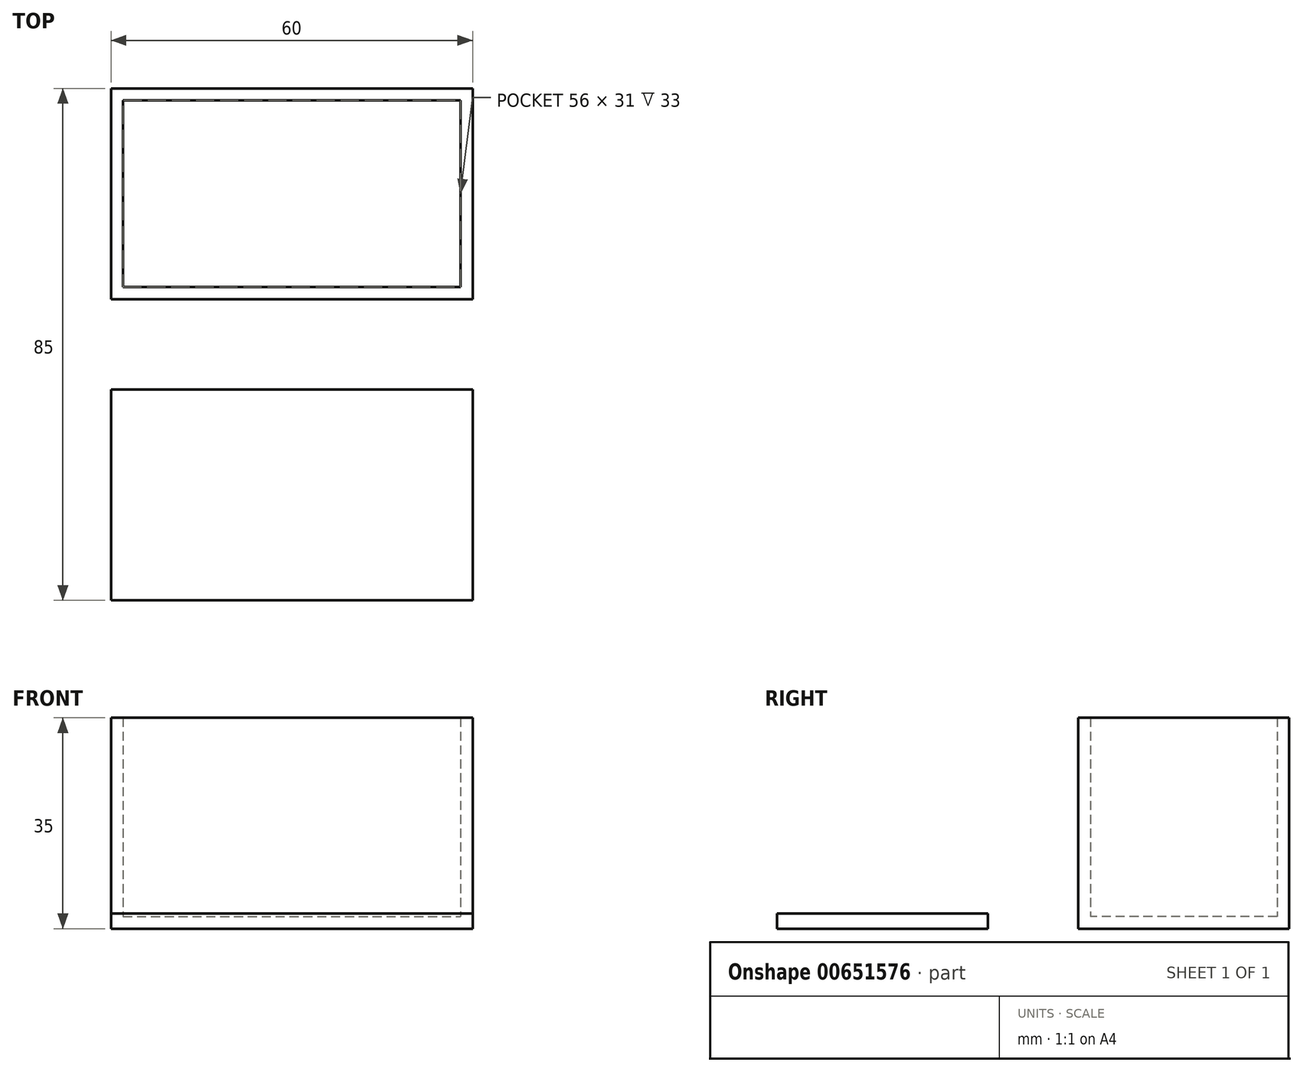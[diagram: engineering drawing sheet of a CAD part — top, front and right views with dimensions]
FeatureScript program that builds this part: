
annotation { "Feature Type Name" : "Feature", "Feature Type Description" : "" }
export const myFeature = defineFeature(function(context is Context, id is Id, definition is map)
    precondition{}
    {
        {
            var Q0;
            Q0=qCreatedBy(makeId("Top.planeOp"),FACE);
            var sketch = newSketch(context, id + "F0", { "sketchPlane" : qUnion([Q0])});
            skLineSegment(sketch, "E0.bottom", {"start": v(-60, 35) * mm, "end": v(0, 35) * mm});
            skLineSegment(sketch, "E0.top", {"start": v(-60, 0) * mm, "end": v(0, 0) * mm});
            skLineSegment(sketch, "E0.left", {"start": v(-60, 35) * mm, "end": v(-60, 0) * mm});
            skLineSegment(sketch, "E0.right", {"start": v(0, 35) * mm, "end": v(0, 0) * mm});
            skSolve(sketch);
        }
        {
            var Q0;
            Q0=makeQuery(id+"F0.imprint","IMPRINT",FACE,{"disambiguationData":[TD([[makeQuery(id+"F0.imprint","IMPRINT",EDGE,{"derivedFrom":sQuery(id+"F0.wireOp",EDGE,"E0.bottom")}),-1.0]])]});
            extrude(context, id + "F1", {"entities" : qUnion([Q0]), "depth" : 35 * mm, "offsetDistance" : 25 * mm});
        }
        {
            var Q0;
            Q0=makeQuery(id+"F1.opExtrude","CAP_FACE",FACE,{"disambiguationData":[OSD([sQuery(id+"F0.wireOp",EDGE,"E0.bottom"),sQuery(id+"F0.wireOp",EDGE,"E0.top"),sQuery(id+"F0.wireOp",EDGE,"E0.left"),sQuery(id+"F0.wireOp",EDGE,"E0.right")])],"isStart":false});
            shell(context, id + "F2", {"entities" : qUnion([Q0]), "thickness" : 2 * mm});
        }
        {
            var Q0;
            Q0=qCreatedBy(makeId("Top.planeOp"),FACE);
            var sketch = newSketch(context, id + "F3", { "sketchPlane" : qUnion([Q0])});
            skLineSegment(sketch, "E1.bottom", {"start": v(-60, -15) * mm, "end": v(0, -15) * mm});
            skLineSegment(sketch, "E1.top", {"start": v(-60, -50) * mm, "end": v(0, -50) * mm});
            skLineSegment(sketch, "E1.left", {"start": v(-60, -15) * mm, "end": v(-60, -50) * mm});
            skLineSegment(sketch, "E1.right", {"start": v(0, -15) * mm, "end": v(0, -50) * mm});
            skSolve(sketch);
        }
        {
            var Q0;
            Q0 = qSketchRegion(id + "F3", true);
            extrude(context, id + "F4", {"entities" : qUnion([Q0]), "depth" : 2.5 * mm, "offsetDistance" : 25 * mm});
        }
        {
            var Q0;
            Q0=makeQuery(id+"F4.opExtrude","SWEPT_BODY",BODY,{"disambiguationData":[OSD([sQuery(id+"F3.wireOp",EDGE,"E1.bottom"),sQuery(id+"F3.wireOp",EDGE,"E1.top"),sQuery(id+"F3.wireOp",EDGE,"E1.left"),sQuery(id+"F3.wireOp",EDGE,"E1.right")])]});
            transform(context, id + "F5", {"entities" : qUnion([Q0]), "transformType" : TransformType.COPY});
        }
    });
